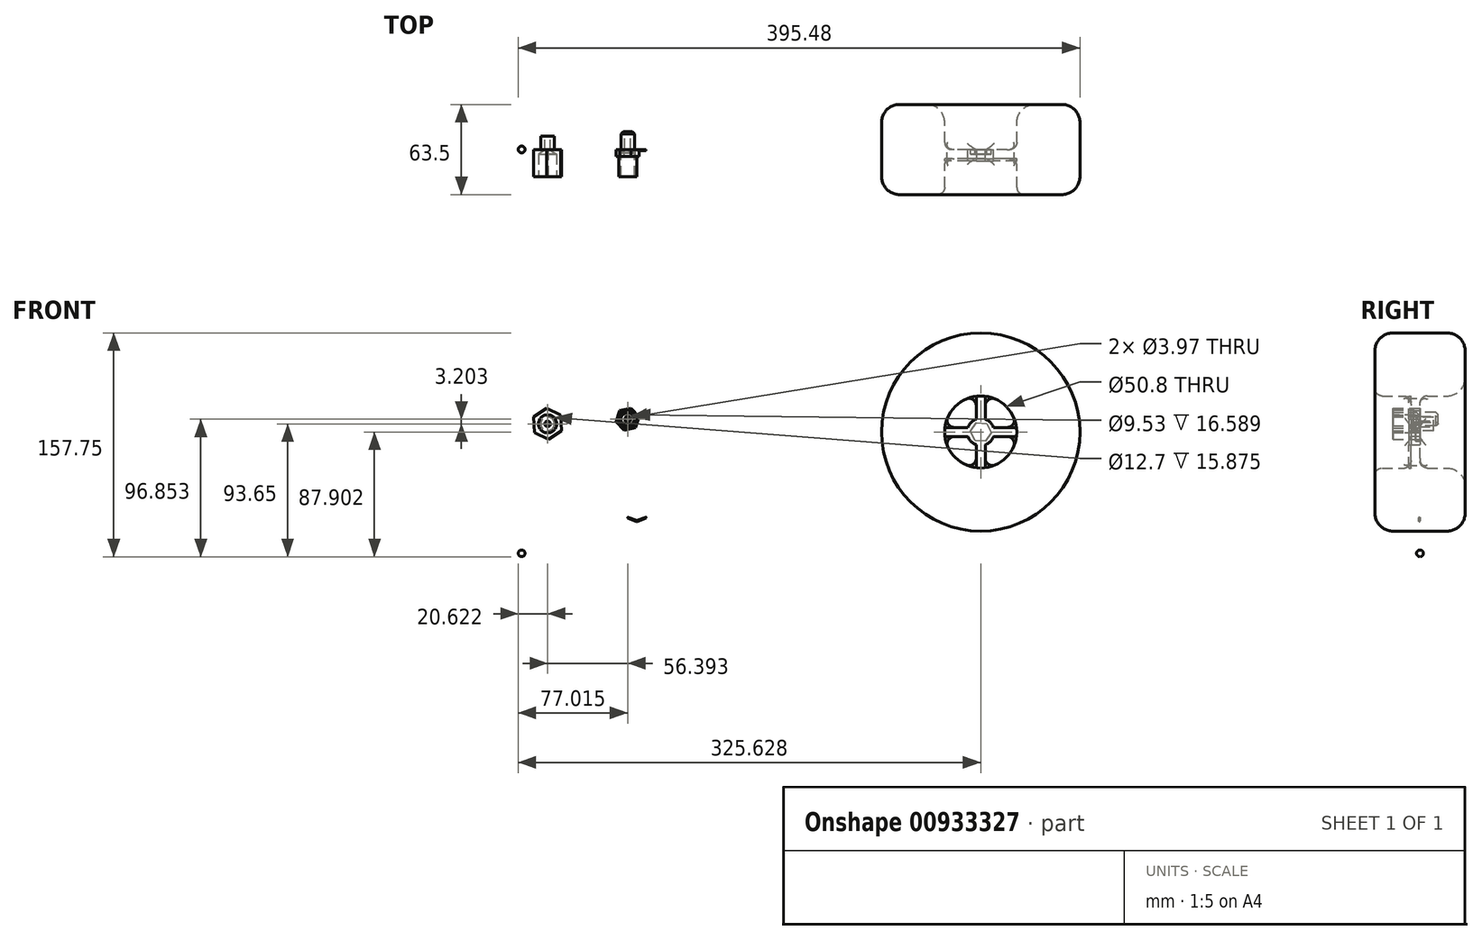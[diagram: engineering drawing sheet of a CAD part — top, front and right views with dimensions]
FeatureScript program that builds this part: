
annotation { "Feature Type Name" : "Feature", "Feature Type Description" : "" }
export const myFeature = defineFeature(function(context is Context, id is Id, definition is map)
    precondition{}
    {
        {
            var Q0;
            Q0=qCreatedBy(makeId("Front.planeOp"),FACE);
            var sketch = newSketch(context, id + "F0", { "sketchPlane" : qUnion([Q0])});
            skCircle(sketch, "E0.cCircle", {"center": v(-37.19, 42.77) * mm, "radius": 11 * mm, "construction": true});
            skLineSegment(sketch, "E0.0", {"start": v(-27.35, 37.85) * mm, "end": v(-36.53, 31.8) * mm});
            skLineSegment(sketch, "E0.1", {"start": v(-36.53, 31.8) * mm, "end": v(-46.37, 36.71) * mm});
            skLineSegment(sketch, "E0.2", {"start": v(-46.37, 36.71) * mm, "end": v(-47.03, 47.69) * mm});
            skLineSegment(sketch, "E0.3", {"start": v(-47.03, 47.69) * mm, "end": v(-37.85, 53.75) * mm});
            skLineSegment(sketch, "E0.4", {"start": v(-37.85, 53.75) * mm, "end": v(-28, 48.83) * mm});
            skLineSegment(sketch, "E0.5", {"start": v(-28, 48.83) * mm, "end": v(-27.35, 37.85) * mm});
            skCircle(sketch, "E1.cCircle", {"center": v(19.2, 45.97) * mm, "radius": 8.25 * mm, "construction": true});
            skLineSegment(sketch, "E1.0", {"start": v(24.83, 39.94) * mm, "end": v(16.8, 38.09) * mm});
            skLineSegment(sketch, "E1.1", {"start": v(16.8, 38.09) * mm, "end": v(11.17, 44.12) * mm});
            skLineSegment(sketch, "E1.2", {"start": v(11.17, 44.12) * mm, "end": v(13.58, 52) * mm});
            skLineSegment(sketch, "E1.3", {"start": v(13.58, 52) * mm, "end": v(21.62, 53.86) * mm});
            skLineSegment(sketch, "E1.4", {"start": v(21.62, 53.86) * mm, "end": v(27.24, 47.83) * mm});
            skLineSegment(sketch, "E1.5", {"start": v(27.24, 47.83) * mm, "end": v(24.83, 39.94) * mm});
            skCircle(sketch, "E2", {"center": v(-37.19, 42.77) * mm, "radius": 4.76 * mm});
            skCircle(sketch, "E3", {"center": v(19.2, 45.97) * mm, "radius": 6.35 * mm});
            skCircle(sketch, "E4", {"center": v(19.2, 45.97) * mm, "radius": 4.76 * mm});
            skCircle(sketch, "E5", {"center": v(19.2, 45.97) * mm, "radius": 1.98 * mm});
            skCircle(sketch, "E6", {"center": v(-37.19, 42.77) * mm, "radius": 1.98 * mm});
            skCircle(sketch, "E7", {"center": v(267.82, 37.02) * mm, "radius": 69.85 * mm});
            skCircle(sketch, "E8", {"center": v(267.82, 37.02) * mm, "radius": 25.4 * mm});
            skLineSegment(sketch, "E9", {"start": v(267.82, 37.02) * mm, "end": v(267.82, 11.62) * mm, "construction": true});
            skLineSegment(sketch, "E10", {"start": v(267.82, 11.62) * mm, "end": v(267.82, 62.42) * mm, "construction": true});
            skLineSegment(sketch, "E11", {"start": v(267.82, 62.42) * mm, "end": v(267.82, 37.02) * mm, "construction": true});
            skLineSegment(sketch, "E12", {"start": v(267.82, 37.02) * mm, "end": v(293.22, 37.02) * mm, "construction": true});
            skLineSegment(sketch, "E13", {"start": v(293.22, 37.02) * mm, "end": v(242.42, 37.02) * mm, "construction": true});
            skLineSegment(sketch, "E14.left", {"start": v(271, 11.82) * mm, "end": v(271, 28.04) * mm});
            skLineSegment(sketch, "E14.right", {"start": v(264.64, 11.82) * mm, "end": v(264.64, 28.04) * mm});
            skLineSegment(sketch, "E15.bottom", {"start": v(293.02, 40.2) * mm, "end": v(276.8, 40.2) * mm});
            skLineSegment(sketch, "E15.top", {"start": v(293.02, 33.85) * mm, "end": v(276.8, 33.85) * mm});
            skArc(sketch, "E16.cCircle", {"start": v(274.43, 40.2) * mm, "mid": v(260.67, 35.4) * mm, "end": v(275.15, 37.02) * mm, "construction": true});
            skLineSegment(sketch, "E16.0", {"start": v(271, 30.41) * mm, "end": v(263.68, 30.97) * mm});
            skLineSegment(sketch, "E16.1", {"start": v(263.68, 30.97) * mm, "end": v(260.5, 37.58) * mm});
            skLineSegment(sketch, "E16.2", {"start": v(260.5, 37.58) * mm, "end": v(264.64, 43.63) * mm});
            skLineSegment(sketch, "E16.3", {"start": v(264.64, 43.63) * mm, "end": v(271.95, 43.08) * mm});
            skLineSegment(sketch, "E16.4", {"start": v(271.95, 43.08) * mm, "end": v(275.13, 36.47) * mm});
            skLineSegment(sketch, "E16.5", {"start": v(275.13, 36.47) * mm, "end": v(271, 30.41) * mm});
            skCircle(sketch, "E17", {"center": v(267.82, 37.02) * mm, "radius": 9.53 * mm});
            skLineSegment(sketch, "E18.trimOffspring", {"start": v(271, 43.63) * mm, "end": v(271, 62.22) * mm});
            skLineSegment(sketch, "E19.trimOffspring", {"start": v(264.64, 43.63) * mm, "end": v(264.64, 62.22) * mm});
            skLineSegment(sketch, "E20.trimOffspring", {"start": v(258.84, 33.85) * mm, "end": v(242.62, 33.85) * mm});
            skLineSegment(sketch, "E21.trimOffspring", {"start": v(258.84, 40.2) * mm, "end": v(242.62, 40.2) * mm});
            skPoint(sketch, "E22.orphan", {"position": v(264.64, 62.42) * mm});
            skPoint(sketch, "E23.orphan", {"position": v(271, 62.42) * mm});
            skPoint(sketch, "E24.orphan", {"position": v(293.22, 33.85) * mm});
            skPoint(sketch, "E15.left.start.orphan", {"position": v(293.22, 40.2) * mm});
            skPoint(sketch, "E25.orphan", {"position": v(271, 11.62) * mm});
            skPoint(sketch, "E26.orphan", {"position": v(264.64, 11.62) * mm});
            skPoint(sketch, "E27.orphan", {"position": v(242.42, 40.2) * mm});
            skPoint(sketch, "E28.orphan", {"position": v(242.42, 33.85) * mm});
            skSolve(sketch);
        }
        {
            var Q0;
            Q0=makeQuery(id+"F0.imprint","IMPRINT",FACE,{"disambiguationData":[TD([[makeQuery(id+"F0.imprint","IMPRINT",EDGE,{"derivedFrom":sQuery(id+"F0.wireOp",EDGE,"E0.0")}),-1.0]])]});
            var Q1;
            Q1=makeQuery(id+"F0.imprint","IMPRINT",FACE,{"disambiguationData":[TD([[makeQuery(id+"F0.imprint","IMPRINT",EDGE,{"derivedFrom":sQuery(id+"F0.wireOp",EDGE,"E2")}),1.0]])]});
            extrude(context, id + "F1", {"entities" : qUnion([Q0, Q1]), "depth" : 19.05 * mm, "offsetDistance" : 25.4 * mm});
        }
        {
            var Q0;
            Q0=makeQuery(id+"F0.imprint","IMPRINT",FACE,{"disambiguationData":[TD([[makeQuery(id+"F0.imprint","IMPRINT",EDGE,{"derivedFrom":sQuery(id+"F0.wireOp",EDGE,"E2")}),1.0]])]});
            extrude(context, id + "F2", {"entities" : qUnion([Q0]), "operationType" : NewBodyOperationType.ADD, "oppositeDirection" : true, "depth" : 9.52 * mm, "offsetDistance" : 25.4 * mm});
        }
        {
            var Q0;
            Q0=makeQuery(id+"F0.imprint","IMPRINT",FACE,{"disambiguationData":[TD([[makeQuery(id+"F0.imprint","IMPRINT",EDGE,{"derivedFrom":sQuery(id+"F0.wireOp",EDGE,"E1.0")}),-1.0]])]});
            var Q1;
            Q1=makeQuery(id+"F0.imprint","IMPRINT",FACE,{"disambiguationData":[TD([[makeQuery(id+"F0.imprint","IMPRINT",EDGE,{"derivedFrom":sQuery(id+"F0.wireOp",EDGE,"E3")}),1.0]])]});
            var Q2;
            Q2=makeQuery(id+"F0.imprint","IMPRINT",FACE,{"disambiguationData":[TD([[makeQuery(id+"F0.imprint","IMPRINT",EDGE,{"derivedFrom":sQuery(id+"F0.wireOp",EDGE,"E4")}),1.0]])]});
            extrude(context, id + "F3", {"entities" : qUnion([Q0, Q1, Q2]), "depth" : 4.76 * mm, "offsetDistance" : 25.4 * mm});
        }
        {
            var Q0;
            Q0=makeQuery(id+"F0.imprint","IMPRINT",FACE,{"disambiguationData":[TD([[makeQuery(id+"F0.imprint","IMPRINT",EDGE,{"derivedFrom":sQuery(id+"F0.wireOp",EDGE,"E4")}),1.0]])]});
            extrude(context, id + "F4", {"entities" : qUnion([Q0]), "operationType" : NewBodyOperationType.ADD, "oppositeDirection" : true, "depth" : 12.7 * mm, "offsetDistance" : 25.4 * mm});
        }
        {
            var Q0;
            Q0=makeQuery(id+"F0.imprint","IMPRINT",FACE,{"disambiguationData":[TD([[makeQuery(id+"F0.imprint","IMPRINT",EDGE,{"derivedFrom":sQuery(id+"F0.wireOp",EDGE,"E3")}),1.0]])]});
            extrude(context, id + "F5", {"entities" : qUnion([Q0]), "operationType" : NewBodyOperationType.ADD, "depth" : 19.05 * mm, "offsetDistance" : 25.4 * mm});
        }
        {
            var Q0;
            Q0=makeQuery(id+"F3.opExtrude","CAP_EDGE",EDGE,{"disambiguationData":[OSD([sQuery(id+"F0.wireOp",EDGE,"E5")])],"isStart":false});
            chamfer(context, id + "F6", {"entities" : qUnion([Q0]), "width" : 5.08 * mm, "tangentPropagation" : true});
        }
        {
            var Q0;
            Q0=makeQuery(id+"F4.opExtrude","CAP_EDGE",EDGE,{"disambiguationData":[OSD([sQuery(id+"F0.wireOp",EDGE,"E4")])],"isStart":false});
            chamfer(context, id + "F7", {"entities" : qUnion([Q0]), "width" : 1.59 * mm, "tangentPropagation" : true});
        }
        {
            var Q0;
            Q0=makeQuery(id+"F1.opExtrude","CAP_FACE",FACE,{"disambiguationData":[OSD([sQuery(id+"F0.wireOp",EDGE,"E0.0"),sQuery(id+"F0.wireOp",EDGE,"E0.1"),sQuery(id+"F0.wireOp",EDGE,"E0.2"),sQuery(id+"F0.wireOp",EDGE,"E0.3"),sQuery(id+"F0.wireOp",EDGE,"E0.4"),sQuery(id+"F0.wireOp",EDGE,"E0.5"),sQuery(id+"F0.wireOp",EDGE,"E6")])],"isStart":false});
            var sketch = newSketch(context, id + "F8", { "sketchPlane" : qUnion([Q0])});
            skCircle(sketch, "E29", {"center": v(-37.19, 42.77) * mm, "radius": 5.43 * mm});
            skSolve(sketch);
        }
        {
            var Q0;
            Q0=sQuery(id+"F8.wireOp",VERTEX,"E29.center");
            var Q1;
            Q1=makeQuery(id+"F1.opExtrude","SWEPT_BODY",BODY,{"disambiguationData":[OSD([sQuery(id+"F0.wireOp",EDGE,"E0.0"),sQuery(id+"F0.wireOp",EDGE,"E0.1"),sQuery(id+"F0.wireOp",EDGE,"E0.2"),sQuery(id+"F0.wireOp",EDGE,"E0.3"),sQuery(id+"F0.wireOp",EDGE,"E0.4"),sQuery(id+"F0.wireOp",EDGE,"E0.5"),sQuery(id+"F0.wireOp",EDGE,"E6")])]});
            hole(context, id + "F9", {"style" : HoleStyle.SIMPLE, "endStyle" : HoleEndStyle.BLIND, "holeDiameter" : 12.7 * mm, "majorDiameter" : 6.35 * mm, "holeDepth" : 15.88 * mm, "isTappedThrough" : true, "tappedDepth" : 12.7 * mm, "tapClearance" : 3, "locations" : qUnion([Q0]), "scope" : qUnion([Q1])});
        }
        {
            var Q0;
            Q0=qCreatedBy(makeId("Front.planeOp"),FACE);
            var sketch = newSketch(context, id + "F10", { "sketchPlane" : qUnion([Q0])});
            skLineSegment(sketch, "E30", {"start": v(-55.43, -56.12) * mm, "end": v(-55.43, -31.19) * mm, "construction": true});
            skCircle(sketch, "E31", {"center": v(-55.43, -48.5) * mm, "radius": 2.38 * mm});
            skLineSegment(sketch, "E32", {"start": v(-55.43, -50.88) * mm, "end": v(-55.43, -46.12) * mm});
            skSolve(sketch);
        }
        {
            var Q0;
            {var subQ0=sQuery(id+"F10.wireOp",EDGE,"E32");Q0=makeQuery(id+"F10.imprint","IMPRINT",FACE,{"disambiguationData":[TD([[makeQuery(id+"F10.imprint","IMPRINT",EDGE,{"derivedFrom":subQ0}),1.0]])]});}
            var Q1;
            Q1=sQuery(id+"F10.wireOp",EDGE,"E30");
            revolve(context, id + "F11", {"surfaceOperationType" : NewSurfaceOperationType.NEW, "entities" : qUnion([Q0]), "axis" : qUnion([Q1]), "revolveType" : RevolveType.FULL});
        }
        {
            var Q0;
            Q0=qCreatedBy(makeId("Front.planeOp"),FACE);
            var sketch = newSketch(context, id + "F12", { "sketchPlane" : qUnion([Q0])});
            skLineSegment(sketch, "E33.bottom", {"start": v(19.43, -22.97) * mm, "end": v(32.13, -22.97) * mm});
            skLineSegment(sketch, "E33.top", {"start": v(19.43, -26.15) * mm, "end": v(32.13, -26.15) * mm});
            skLineSegment(sketch, "E33.left", {"start": v(19.43, -22.97) * mm, "end": v(19.43, -26.15) * mm});
            skLineSegment(sketch, "E33.right", {"start": v(32.13, -22.97) * mm, "end": v(32.13, -26.15) * mm});
            skLineSegment(sketch, "E34", {"start": v(25.78, -26.15) * mm, "end": v(32.13, -23.8) * mm});
            skLineSegment(sketch, "E35", {"start": v(25.78, -26.15) * mm, "end": v(19.43, -23.8) * mm});
            skLineSegment(sketch, "E36", {"start": v(19.43, -22.97) * mm, "end": v(25.78, -25.32) * mm});
            skLineSegment(sketch, "E37", {"start": v(25.78, -25.32) * mm, "end": v(32.13, -22.97) * mm});
            skSolve(sketch);
        }
        {
            var Q0;
            {var subQ0=sQuery(id+"F12.wireOp",EDGE,"E34");Q0=makeQuery(id+"F12.imprint","IMPRINT",FACE,{"disambiguationData":[TD([[makeQuery(id+"F12.imprint","IMPRINT",EDGE,{"derivedFrom":subQ0}),1.0]])]});}
            extrude(context, id + "F13", {"entities" : qUnion([Q0]), "depth" : 0.83 * mm, "offsetDistance" : 25.4 * mm});
        }
        {
            var Q0;
            Q0=makeQuery(id+"F13.opExtrude","CAP_FACE",FACE,{"disambiguationData":[OSD([sQuery(id+"F12.wireOp",EDGE,"E33.left"),sQuery(id+"F12.wireOp",EDGE,"E33.right"),sQuery(id+"F12.wireOp",EDGE,"E34"),sQuery(id+"F12.wireOp",EDGE,"E35"),sQuery(id+"F12.wireOp",EDGE,"E36"),sQuery(id+"F12.wireOp",EDGE,"E37")])],"isStart":false});
            var Q1;
            Q1=makeQuery(id+"F13.opExtrude","CAP_FACE",FACE,{"disambiguationData":[OSD([sQuery(id+"F12.wireOp",EDGE,"E33.left"),sQuery(id+"F12.wireOp",EDGE,"E33.right"),sQuery(id+"F12.wireOp",EDGE,"E34"),sQuery(id+"F12.wireOp",EDGE,"E35"),sQuery(id+"F12.wireOp",EDGE,"E36"),sQuery(id+"F12.wireOp",EDGE,"E37")])],"isStart":true});
            fillet(context, id + "F14", {"entities" : qUnion([Q0, Q1]), "radius" : 0.38 * mm, "tangentPropagation" : true, "allowEdgeOverflow" : false});
        }
        {
            var Q0;
            Q0=makeQuery(id+"F0.imprint","IMPRINT",FACE,{"disambiguationData":[TD([[makeQuery(id+"F0.imprint","IMPRINT",EDGE,{"derivedFrom":sQuery(id+"F0.wireOp",EDGE,"E7")}),1.0]])]});
            extrude(context, id + "F15", {"entities" : qUnion([Q0]), "depth" : 31.75 * mm, "offsetDistance" : 25.4 * mm});
        }
        {
            var Q0;
            Q0=makeQuery(id+"F0.imprint","IMPRINT",FACE,{"disambiguationData":[TD([[makeQuery(id+"F0.imprint","IMPRINT",EDGE,{"derivedFrom":sQuery(id+"F0.wireOp",EDGE,"E7")}),1.0]])]});
            extrude(context, id + "F16", {"entities" : qUnion([Q0]), "operationType" : NewBodyOperationType.ADD, "oppositeDirection" : true, "depth" : 31.75 * mm, "offsetDistance" : 25.4 * mm});
        }
        {
            var Q0;
            {var subQ0=sQuery(id+"F0.wireOp",EDGE,"E18.trimOffspring");var subQ1=sQuery(id+"F0.wireOp",EDGE,"E8");var subQ2=makeQuery(id+"F0.imprint","INTERSECT",VERTEX,{"derivedFrom":[subQ1,subQ0]});Q0=makeQuery(id+"F0.imprint","IMPRINT",FACE,{"disambiguationData":[TD([[makeQuery(id+"F0.imprint","IMPRINT",EDGE,{"disambiguationData":[TD([[subQ2,-1.0]])],"derivedFrom":subQ1}),1.0]])]});}
            var Q1;
            {var subQ0=sQuery(id+"F0.wireOp",EDGE,"E20.trimOffspring");Q1=makeQuery(id+"F0.imprint","IMPRINT",FACE,{"disambiguationData":[TD([[makeQuery(id+"F0.imprint","IMPRINT",EDGE,{"derivedFrom":subQ0}),-1.0]])]});}
            var Q2;
            Q2=makeQuery(id+"F0.imprint","IMPRINT",FACE,{"disambiguationData":[TD([[makeQuery(id+"F0.imprint","IMPRINT",EDGE,{"derivedFrom":sQuery(id+"F0.wireOp",EDGE,"E16.0")}),1.0]])]});
            var Q3;
            {var subQ0=sQuery(id+"F0.wireOp",EDGE,"E15.bottom");Q3=makeQuery(id+"F0.imprint","IMPRINT",FACE,{"disambiguationData":[TD([[makeQuery(id+"F0.imprint","IMPRINT",EDGE,{"derivedFrom":subQ0}),1.0]])]});}
            var Q4;
            {var subQ0=sQuery(id+"F0.wireOp",EDGE,"E14.left");Q4=makeQuery(id+"F0.imprint","IMPRINT",FACE,{"disambiguationData":[TD([[makeQuery(id+"F0.imprint","IMPRINT",EDGE,{"derivedFrom":subQ0}),1.0]])]});}
            extrude(context, id + "F17", {"entities" : qUnion([Q0, Q1, Q2, Q3, Q4]), "operationType" : NewBodyOperationType.ADD, "depth" : 6.35 * mm, "offsetDistance" : 25.4 * mm});
        }
        {
            var Q0;
            {var subQ0=sQuery(id+"F0.wireOp",EDGE,"E14.left");Q0=makeQuery(id+"F0.imprint","IMPRINT",FACE,{"disambiguationData":[TD([[makeQuery(id+"F0.imprint","IMPRINT",EDGE,{"derivedFrom":subQ0}),1.0]])]});}
            var Q1;
            {var subQ0=sQuery(id+"F0.wireOp",EDGE,"E18.trimOffspring");var subQ1=sQuery(id+"F0.wireOp",EDGE,"E8");var subQ2=makeQuery(id+"F0.imprint","INTERSECT",VERTEX,{"derivedFrom":[subQ1,subQ0]});Q1=makeQuery(id+"F0.imprint","IMPRINT",FACE,{"disambiguationData":[TD([[makeQuery(id+"F0.imprint","IMPRINT",EDGE,{"disambiguationData":[TD([[subQ2,-1.0]])],"derivedFrom":subQ1}),1.0]])]});}
            var Q2;
            Q2=makeQuery(id+"F0.imprint","IMPRINT",FACE,{"disambiguationData":[TD([[makeQuery(id+"F0.imprint","IMPRINT",EDGE,{"derivedFrom":sQuery(id+"F0.wireOp",EDGE,"E16.0")}),1.0]])]});
            var Q3;
            {var subQ0=sQuery(id+"F0.wireOp",EDGE,"E15.bottom");Q3=makeQuery(id+"F0.imprint","IMPRINT",FACE,{"disambiguationData":[TD([[makeQuery(id+"F0.imprint","IMPRINT",EDGE,{"derivedFrom":subQ0}),1.0]])]});}
            var Q4;
            {var subQ0=sQuery(id+"F0.wireOp",EDGE,"E20.trimOffspring");Q4=makeQuery(id+"F0.imprint","IMPRINT",FACE,{"disambiguationData":[TD([[makeQuery(id+"F0.imprint","IMPRINT",EDGE,{"derivedFrom":subQ0}),-1.0]])]});}
            extrude(context, id + "F18", {"entities" : qUnion([Q0, Q1, Q2, Q3, Q4]), "operationType" : NewBodyOperationType.ADD, "depth" : 6.35 * mm, "offsetDistance" : 25.4 * mm});
        }
        {
            var Q0;
            Q0=makeQuery(id+"F17.opExtrude","CAP_FACE",FACE,{"disambiguationData":[OSD([sQuery(id+"F0.wireOp",EDGE,"E8"),sQuery(id+"F0.wireOp",EDGE,"E14.left"),sQuery(id+"F0.wireOp",EDGE,"E14.right"),sQuery(id+"F0.wireOp",EDGE,"E15.bottom"),sQuery(id+"F0.wireOp",EDGE,"E15.top"),sQuery(id+"F0.wireOp",EDGE,"E16.0"),sQuery(id+"F0.wireOp",EDGE,"E16.1"),sQuery(id+"F0.wireOp",EDGE,"E16.2"),sQuery(id+"F0.wireOp",EDGE,"E16.3"),sQuery(id+"F0.wireOp",EDGE,"E16.4"),sQuery(id+"F0.wireOp",EDGE,"E16.5"),sQuery(id+"F0.wireOp",EDGE,"E17"),sQuery(id+"F0.wireOp",EDGE,"E18.trimOffspring"),sQuery(id+"F0.wireOp",EDGE,"E19.trimOffspring"),sQuery(id+"F0.wireOp",EDGE,"E20.trimOffspring"),sQuery(id+"F0.wireOp",EDGE,"E21.trimOffspring")])],"isStart":false});
            var sketch = newSketch(context, id + "F19", { "sketchPlane" : qUnion([Q0])});
            skCircle(sketch, "E38", {"center": v(267.82, 37.02) * mm, "radius": 7.33 * mm});
            skSolve(sketch);
        }
        {
            var Q0;
            {var subQ1=makeQuery(id+"F17.opExtrude","CAP_EDGE",EDGE,{"disambiguationData":[OSD([sQuery(id+"F0.wireOp",EDGE,"E16.1")])],"isStart":false});Q0=makeQuery(id+"F19.imprint","IMPRINT",FACE,{"disambiguationData":[TD([[makeQuery(id+"F19.imprint","IMPRINT",EDGE,{"derivedFrom":subQ1}),1.0]])]});}
            var Q1;
            {var subQ1=makeQuery(id+"F17.opExtrude","CAP_EDGE",EDGE,{"disambiguationData":[OSD([sQuery(id+"F0.wireOp",EDGE,"E16.5")])],"isStart":false});Q1=makeQuery(id+"F19.imprint","IMPRINT",FACE,{"disambiguationData":[TD([[makeQuery(id+"F19.imprint","IMPRINT",EDGE,{"derivedFrom":subQ1}),1.0]])]});}
            var Q2;
            Q2=makeQuery(id+"F19.imprint","IMPRINT",FACE,{"disambiguationData":[TD([[makeQuery(id+"F19.imprint","IMPRINT",EDGE,{"derivedFrom":makeQuery(id+"F17.opExtrude","CAP_EDGE",EDGE,{"disambiguationData":[OSD([sQuery(id+"F0.wireOp",EDGE,"E16.0")])],"isStart":false})}),-1.0]])]});
            var Q3;
            {var subQ1=makeQuery(id+"F17.opExtrude","CAP_EDGE",EDGE,{"disambiguationData":[OSD([sQuery(id+"F0.wireOp",EDGE,"E16.4")])],"isStart":false});Q3=makeQuery(id+"F19.imprint","IMPRINT",FACE,{"disambiguationData":[TD([[makeQuery(id+"F19.imprint","IMPRINT",EDGE,{"derivedFrom":subQ1}),1.0]])]});}
            var Q4;
            {var subQ1=makeQuery(id+"F17.opExtrude","CAP_EDGE",EDGE,{"disambiguationData":[OSD([sQuery(id+"F0.wireOp",EDGE,"E16.3")])],"isStart":false});Q4=makeQuery(id+"F19.imprint","IMPRINT",FACE,{"disambiguationData":[TD([[makeQuery(id+"F19.imprint","IMPRINT",EDGE,{"derivedFrom":subQ1}),1.0]])]});}
            var Q5;
            {var subQ1=makeQuery(id+"F17.opExtrude","CAP_EDGE",EDGE,{"disambiguationData":[OSD([sQuery(id+"F0.wireOp",EDGE,"E16.2")])],"isStart":false});Q5=makeQuery(id+"F19.imprint","IMPRINT",FACE,{"disambiguationData":[TD([[makeQuery(id+"F19.imprint","IMPRINT",EDGE,{"derivedFrom":subQ1}),1.0]])]});}
            var Q6;
            {var subQ1=makeQuery(id+"F17.opExtrude","CAP_EDGE",EDGE,{"disambiguationData":[OSD([sQuery(id+"F0.wireOp",EDGE,"E16.0")])],"isStart":false});Q6=makeQuery(id+"F19.imprint","IMPRINT",FACE,{"disambiguationData":[TD([[makeQuery(id+"F19.imprint","IMPRINT",EDGE,{"derivedFrom":subQ1}),1.0]])]});}
            extrude(context, id + "F20", {"entities" : qUnion([Q0, Q1, Q2, Q3, Q4, Q5, Q6]), "operationType" : NewBodyOperationType.ADD, "oppositeDirection" : true, "depth" : 3.17 * mm, "offsetDistance" : 25.4 * mm});
        }
        {
            var Q0;
            Q0=makeQuery(id+"F15.opExtrude","CAP_EDGE",EDGE,{"disambiguationData":[OSD([sQuery(id+"F0.wireOp",EDGE,"E7")])],"isStart":false});
            var Q1;
            Q1=makeQuery(id+"F16.opExtrude","CAP_FACE",FACE,{"disambiguationData":[OSD([sQuery(id+"F0.wireOp",EDGE,"E7"),sQuery(id+"F0.wireOp",EDGE,"E8")])],"isStart":false});
            fillet(context, id + "F21", {"entities" : qUnion([Q0, Q1]), "tangentPropagation" : true, "radius" : 12.7 * mm, "defaultsChanged" : false, "vertexSettings" : [], "allowEdgeOverflow" : false});
        }
        {
            var Q0;
            Q0=makeQuery(id+"F20.boolean.opBoolean","MERGE",FACE,{"derivedFrom":[makeQuery(id+"F17.opExtrude","CAP_FACE",FACE,{"disambiguationData":[OSD([sQuery(id+"F0.wireOp",EDGE,"E8"),sQuery(id+"F0.wireOp",EDGE,"E14.left"),sQuery(id+"F0.wireOp",EDGE,"E14.right"),sQuery(id+"F0.wireOp",EDGE,"E15.bottom"),sQuery(id+"F0.wireOp",EDGE,"E15.top"),sQuery(id+"F0.wireOp",EDGE,"E16.0"),sQuery(id+"F0.wireOp",EDGE,"E16.1"),sQuery(id+"F0.wireOp",EDGE,"E16.2"),sQuery(id+"F0.wireOp",EDGE,"E16.3"),sQuery(id+"F0.wireOp",EDGE,"E16.4"),sQuery(id+"F0.wireOp",EDGE,"E16.5"),sQuery(id+"F0.wireOp",EDGE,"E17"),sQuery(id+"F0.wireOp",EDGE,"E18.trimOffspring"),sQuery(id+"F0.wireOp",EDGE,"E19.trimOffspring"),sQuery(id+"F0.wireOp",EDGE,"E20.trimOffspring"),sQuery(id+"F0.wireOp",EDGE,"E21.trimOffspring")])],"isStart":false}),makeQuery(id+"F20.opExtrude","CAP_FACE",FACE,{"disambiguationData":[OSD([sQuery(id+"F19.wireOp",EDGE,"E38")])],"isStart":true})]});
            extrude(context, id + "F22", {"entities" : qUnion([Q0]), "depth" : 1.59 * mm, "offsetDistance" : 25.4 * mm});
        }
        {
            var Q0;
            {var subQ0=sQuery(id+"F0.wireOp",EDGE,"E8");Q0=makeQuery(id+"F16.boolean.opBoolean","MERGE",FACE,{"derivedFrom":[makeQuery(id+"F15.opExtrude","SWEPT_FACE",FACE,{"disambiguationData":[OSD([subQ0])]}),makeQuery(id+"F16.opExtrude","SWEPT_FACE",FACE,{"disambiguationData":[OSD([subQ0])]})]});}
            fillet(context, id + "F23", {"entities" : qUnion([Q0]), "tangentPropagation" : true, "radius" : 5.08 * mm, "defaultsChanged" : false, "vertexSettings" : [], "allowEdgeOverflow" : false});
        }
    });
